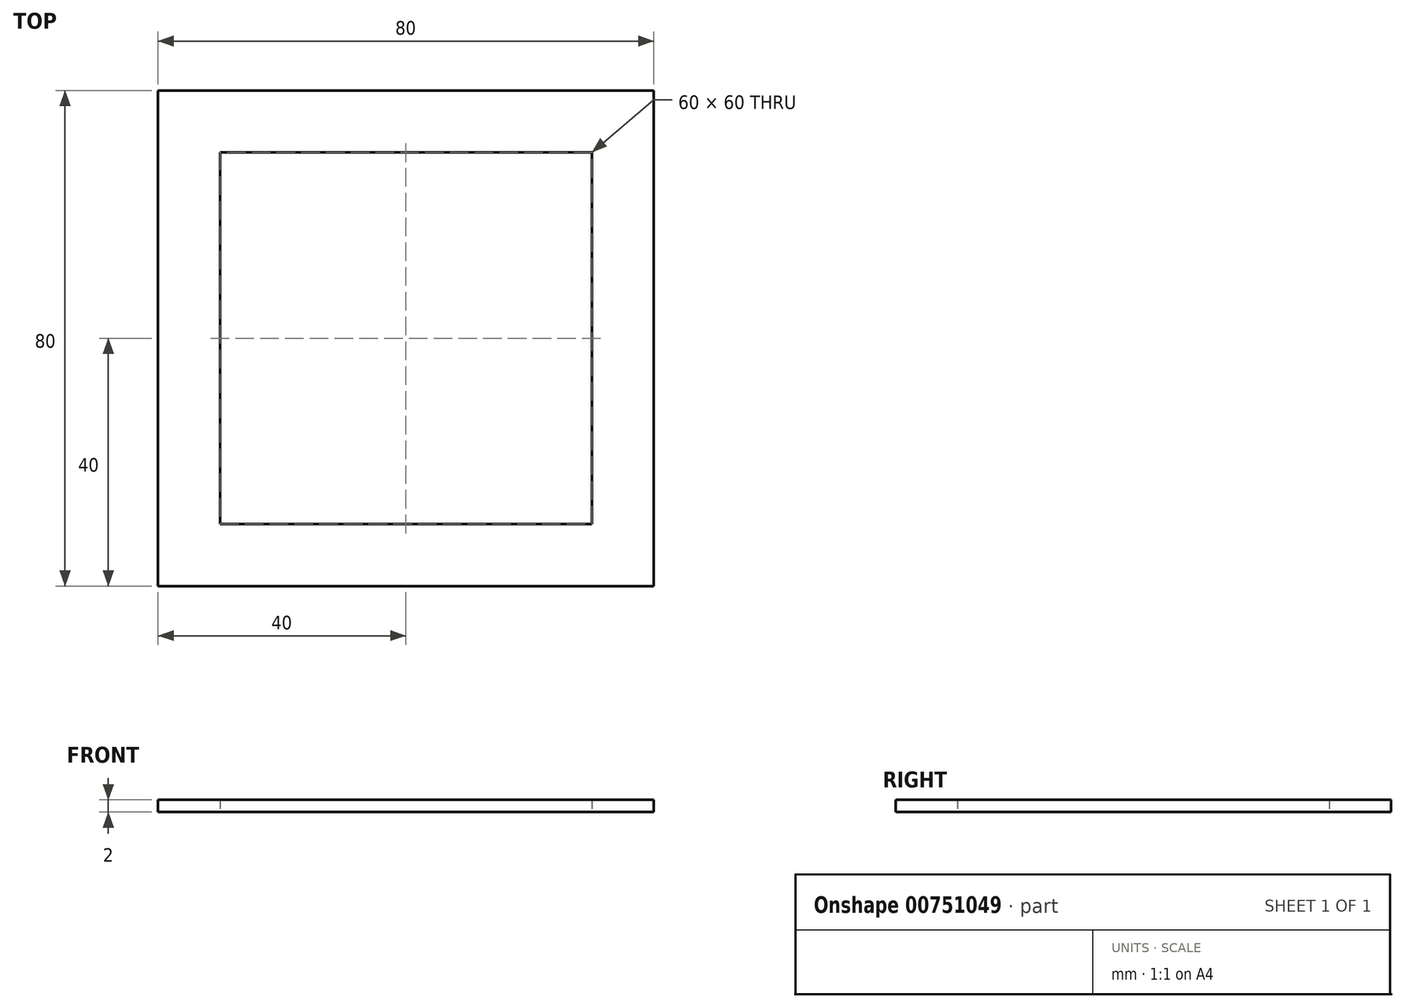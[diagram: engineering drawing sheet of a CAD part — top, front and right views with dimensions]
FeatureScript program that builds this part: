
annotation { "Feature Type Name" : "Feature", "Feature Type Description" : "" }
export const myFeature = defineFeature(function(context is Context, id is Id, definition is map)
    precondition{}
    {
        {
            var Q0;
            Q0=qCreatedBy(makeId("Top.planeOp"),FACE);
            var sketch = newSketch(context, id + "F0", { "sketchPlane" : qUnion([Q0])});
            skLineSegment(sketch, "E0.bottom", {"start": v(40, -40) * mm, "end": v(-40, -40) * mm});
            skLineSegment(sketch, "E0.top", {"start": v(40, 40) * mm, "end": v(-40, 40) * mm});
            skLineSegment(sketch, "E0.left", {"start": v(40, -40) * mm, "end": v(40, 40) * mm});
            skLineSegment(sketch, "E0.right", {"start": v(-40, -40) * mm, "end": v(-40, 40) * mm});
            skPoint(sketch, "E0.middle", {"position": v(0, 0) * mm});
            skLineSegment(sketch, "E1.bottom", {"start": v(30, 30) * mm, "end": v(-30, 30) * mm});
            skLineSegment(sketch, "E1.top", {"start": v(30, -30) * mm, "end": v(-30, -30) * mm});
            skLineSegment(sketch, "E1.left", {"start": v(30, 30) * mm, "end": v(30, -30) * mm});
            skLineSegment(sketch, "E1.right", {"start": v(-30, 30) * mm, "end": v(-30, -30) * mm});
            skSolve(sketch);
        }
        {
            var Q0;
            Q0 = qSketchRegion(id + "F0", true);
            extrude(context, id + "F1", {"entities" : qUnion([Q0]), "depth" : 2 * mm, "offsetDistance" : 25 * mm});
        }
    });
